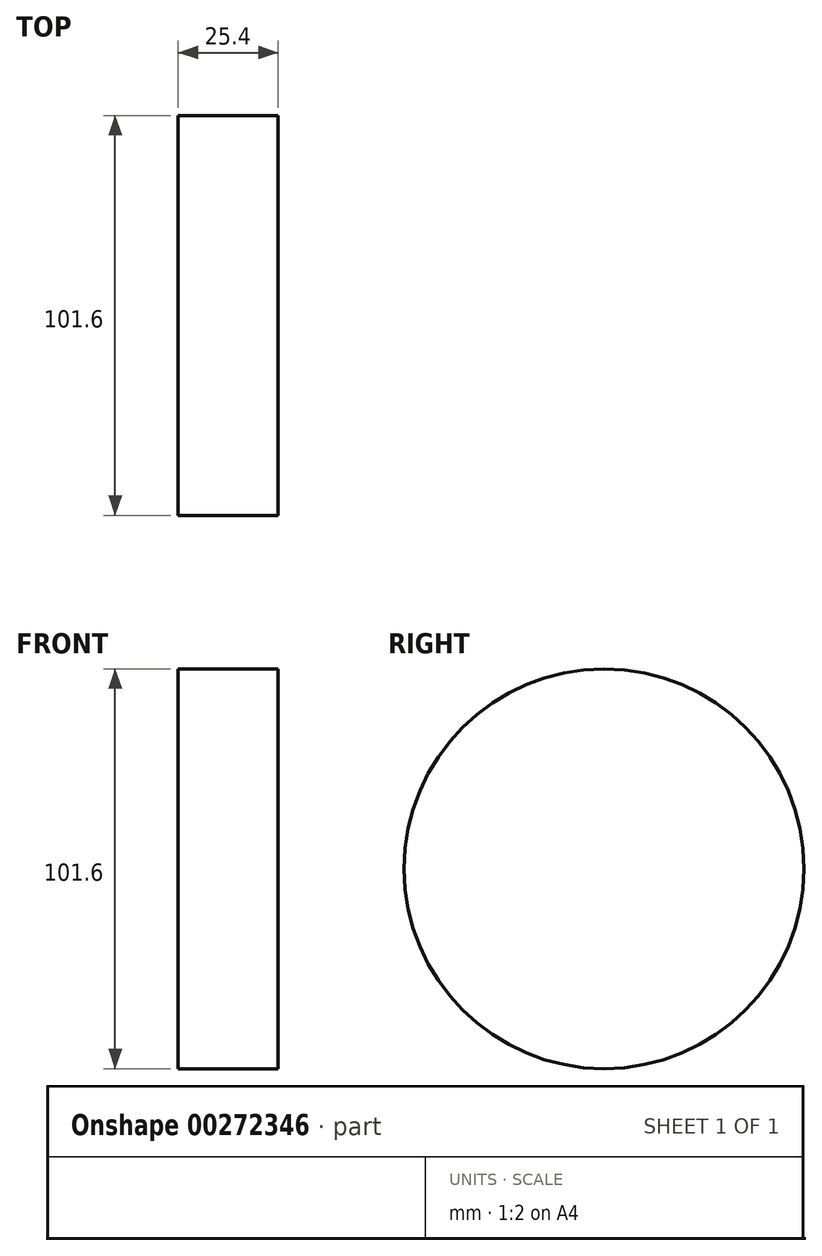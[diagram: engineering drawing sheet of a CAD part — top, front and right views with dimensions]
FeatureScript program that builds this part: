
annotation { "Feature Type Name" : "Feature", "Feature Type Description" : "" }
export const myFeature = defineFeature(function(context is Context, id is Id, definition is map)
    precondition{}
    {
        {
            var Q0;
            Q0=qCreatedBy(makeId("Right.planeOp"),FACE);
            var sketch = newSketch(context, id + "F0", { "sketchPlane" : qUnion([Q0])});
            skCircle(sketch, "E0", {"center": v(0, 0) * mm, "radius": 50.8 * mm});
            skSolve(sketch);
        }
        {
            var Q0;
            Q0=makeQuery(id+"F0.imprint","IMPRINT",FACE,{"disambiguationData":[TD([[makeQuery(id+"F0.imprint","IMPRINT",EDGE,{"derivedFrom":sQuery(id+"F0.wireOp",EDGE,"E0")}),1.0]])]});
            extrude(context, id + "F1", {"entities" : qUnion([Q0]), "depth" : 25.4 * mm});
        }
    });
